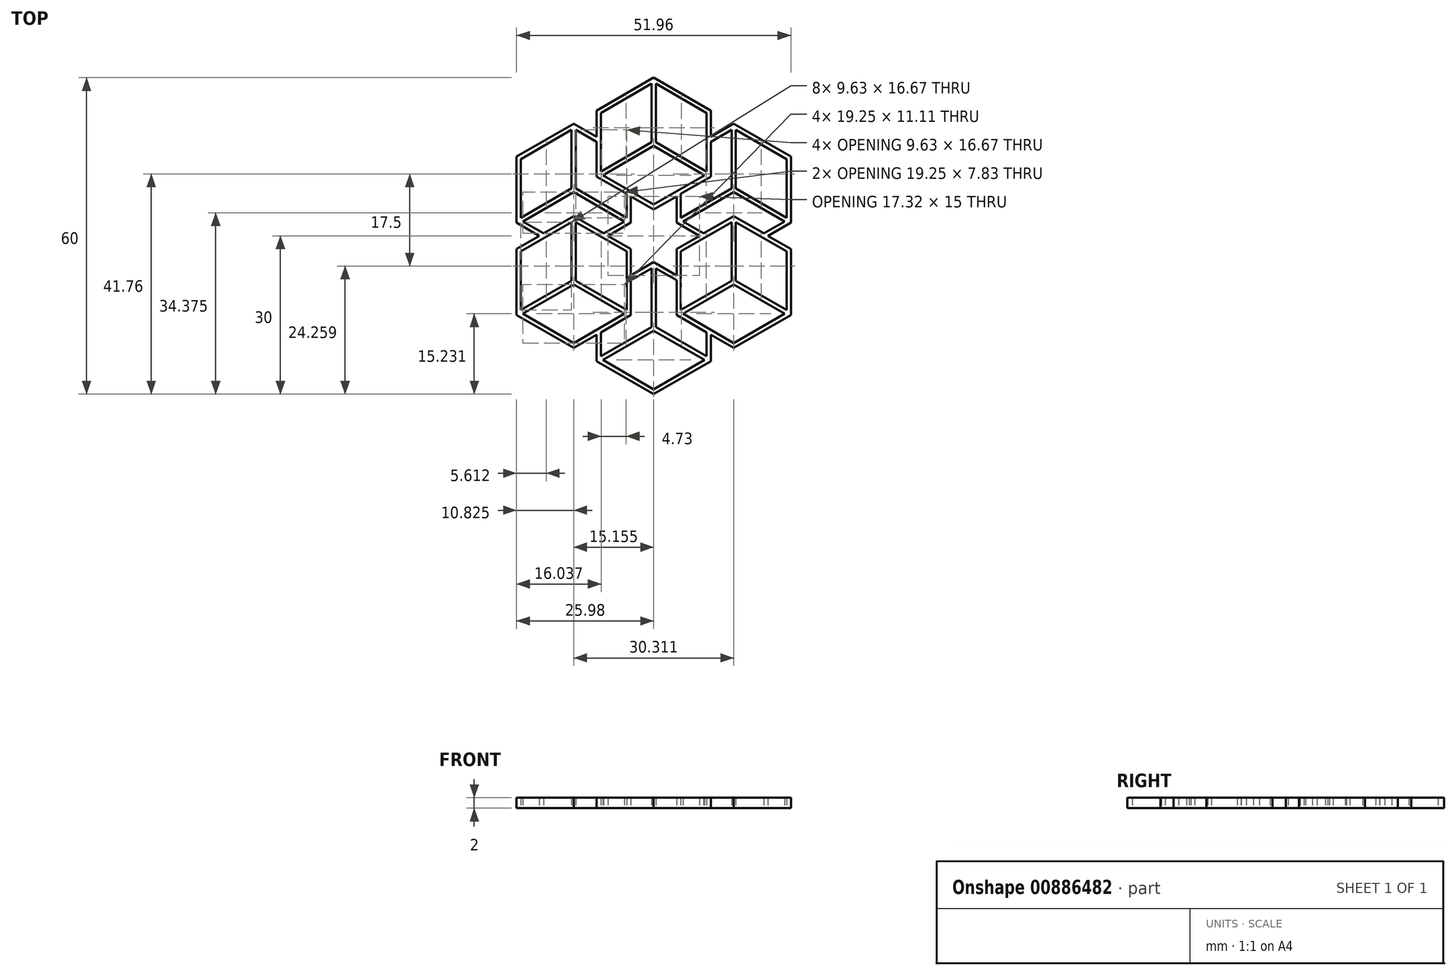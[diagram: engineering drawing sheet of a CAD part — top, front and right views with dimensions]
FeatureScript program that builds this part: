
annotation { "Feature Type Name" : "Feature", "Feature Type Description" : "" }
export const myFeature = defineFeature(function(context is Context, id is Id, definition is map)
    precondition{}
    {
        {
            var Q0;
            Q0=qCreatedBy(makeId("Top.planeOp"),FACE);
            var sketch = newSketch(context, id + "F0", { "sketchPlane" : qUnion([Q0])});
            skCircle(sketch, "E0.cCircle", {"center": v(0, 0) * mm, "radius": 30 * mm, "construction": true});
            skLineSegment(sketch, "E0.0", {"start": v(-25.98, 15) * mm, "end": v(0, 30) * mm, "construction": true});
            skLineSegment(sketch, "E0.1", {"start": v(0, 30) * mm, "end": v(25.98, 15) * mm, "construction": true});
            skLineSegment(sketch, "E0.2", {"start": v(25.98, 15) * mm, "end": v(25.98, -15) * mm, "construction": true});
            skLineSegment(sketch, "E0.3", {"start": v(25.98, -15) * mm, "end": v(0, -30) * mm, "construction": true});
            skLineSegment(sketch, "E0.4", {"start": v(0, -30) * mm, "end": v(-25.98, -15) * mm, "construction": true});
            skLineSegment(sketch, "E0.5", {"start": v(-25.98, -15) * mm, "end": v(-25.98, 15) * mm, "construction": true});
            skCircle(sketch, "E1.cCircle", {"center": v(0, -17.5) * mm, "radius": 12.5 * mm, "construction": true});
            skLineSegment(sketch, "E1.0", {"start": v(0, -30) * mm, "end": v(-10.83, -23.75) * mm});
            skLineSegment(sketch, "E1.1", {"start": v(-10.83, -23.75) * mm, "end": v(-10.83, -11.25) * mm});
            skLineSegment(sketch, "E1.2", {"start": v(-10.83, -11.25) * mm, "end": v(0, -5) * mm});
            skLineSegment(sketch, "E1.3", {"start": v(0, -5) * mm, "end": v(10.83, -11.25) * mm});
            skLineSegment(sketch, "E1.4", {"start": v(10.83, -11.25) * mm, "end": v(10.83, -23.75) * mm});
            skLineSegment(sketch, "E1.5", {"start": v(10.83, -23.75) * mm, "end": v(0, -30) * mm});
            skCircle(sketch, "E2.cCircle", {"center": v(0, -17.5) * mm, "radius": 11.58 * mm, "construction": true});
            skLineSegment(sketch, "E2.0", {"start": v(0.4, -6.15) * mm, "end": v(10.03, -11.71) * mm});
            skLineSegment(sketch, "E2.1", {"start": v(10.03, -11.71) * mm, "end": v(10.03, -22.83) * mm});
            skLineSegment(sketch, "E2.2", {"start": v(9.63, -23.52) * mm, "end": v(0, -29.08) * mm});
            skLineSegment(sketch, "E2.3", {"start": v(0, -29.08) * mm, "end": v(-9.63, -23.52) * mm});
            skLineSegment(sketch, "E2.4", {"start": v(-10.03, -22.83) * mm, "end": v(-10.03, -11.71) * mm});
            skLineSegment(sketch, "E2.5", {"start": v(-10.03, -11.71) * mm, "end": v(-0.4, -6.15) * mm});
            skLineSegment(sketch, "E3.0", {"start": v(0, -17.96) * mm, "end": v(9.63, -23.52) * mm});
            skLineSegment(sketch, "E4.0", {"start": v(0.4, -17.27) * mm, "end": v(10.03, -22.83) * mm});
            skLineSegment(sketch, "E5.0", {"start": v(-0.4, -17.27) * mm, "end": v(-10.03, -22.83) * mm});
            skLineSegment(sketch, "E6.0", {"start": v(0, -17.96) * mm, "end": v(-9.63, -23.52) * mm});
            skPoint(sketch, "E7.orphan", {"position": v(-10.03, -23.29) * mm});
            skLineSegment(sketch, "E8.trimOffspring", {"start": v(-0.4, -6.15) * mm, "end": v(-0.4, -17.27) * mm});
            skLineSegment(sketch, "E9.trimOffspring", {"start": v(0.4, -6.15) * mm, "end": v(0.4, -17.27) * mm});
            skPoint(sketch, "E10.orphan", {"position": v(0, -5.92) * mm});
            skLineSegment(sketch, "E11", {"start": v(0, -17.5) * mm, "end": v(10.83, -23.75) * mm, "construction": true});
            skLineSegment(sketch, "E12", {"start": v(0, -17.5) * mm, "end": v(-10.83, -23.75) * mm, "construction": true});
            skCircle(sketch, "E13.cCircle", {"center": v(15.16, -8.75) * mm, "radius": 12.5 * mm, "construction": true});
            skLineSegment(sketch, "E13.0", {"start": v(15.16, -21.25) * mm, "end": v(4.33, -15) * mm});
            skLineSegment(sketch, "E13.1", {"start": v(4.33, -15) * mm, "end": v(4.33, -2.5) * mm});
            skLineSegment(sketch, "E13.2", {"start": v(4.33, -2.5) * mm, "end": v(15.16, 3.75) * mm});
            skLineSegment(sketch, "E13.3", {"start": v(15.16, 3.75) * mm, "end": v(25.98, -2.5) * mm});
            skLineSegment(sketch, "E13.4", {"start": v(25.98, -2.5) * mm, "end": v(25.98, -15) * mm});
            skLineSegment(sketch, "E13.5", {"start": v(25.98, -15) * mm, "end": v(15.16, -21.25) * mm});
            skCircle(sketch, "E14.cCircle", {"center": v(15.16, -8.75) * mm, "radius": 11.58 * mm, "construction": true});
            skLineSegment(sketch, "E14.0", {"start": v(15.56, 2.6) * mm, "end": v(25.18, -2.96) * mm});
            skLineSegment(sketch, "E14.1", {"start": v(25.18, -2.96) * mm, "end": v(25.18, -14.08) * mm});
            skLineSegment(sketch, "E14.2", {"start": v(24.78, -14.77) * mm, "end": v(15.16, -20.33) * mm});
            skLineSegment(sketch, "E14.3", {"start": v(15.16, -20.33) * mm, "end": v(5.53, -14.77) * mm});
            skLineSegment(sketch, "E14.4", {"start": v(5.13, -14.08) * mm, "end": v(5.13, -2.96) * mm});
            skLineSegment(sketch, "E14.5", {"start": v(5.13, -2.96) * mm, "end": v(14.76, 2.6) * mm});
            skLineSegment(sketch, "E15.0", {"start": v(15.16, -9.21) * mm, "end": v(24.78, -14.77) * mm});
            skLineSegment(sketch, "E16.0", {"start": v(15.56, -8.52) * mm, "end": v(25.18, -14.08) * mm});
            skLineSegment(sketch, "E17.0", {"start": v(14.76, -8.52) * mm, "end": v(5.13, -14.08) * mm});
            skLineSegment(sketch, "E18.0", {"start": v(15.16, -9.21) * mm, "end": v(5.53, -14.77) * mm});
            skPoint(sketch, "E19.orphan", {"position": v(5.13, -14.54) * mm});
            skLineSegment(sketch, "E20.trimOffspring", {"start": v(14.76, 2.6) * mm, "end": v(14.76, -8.52) * mm});
            skLineSegment(sketch, "E21.trimOffspring", {"start": v(15.56, 2.6) * mm, "end": v(15.56, -8.52) * mm});
            skPoint(sketch, "E22.orphan", {"position": v(15.16, 2.83) * mm});
            skLineSegment(sketch, "E23", {"start": v(15.16, -8.75) * mm, "end": v(25.98, -15) * mm, "construction": true});
            skLineSegment(sketch, "E24", {"start": v(15.16, -8.75) * mm, "end": v(4.33, -15) * mm, "construction": true});
            skCircle(sketch, "E25.cCircle", {"center": v(-15.16, -8.75) * mm, "radius": 12.5 * mm, "construction": true});
            skLineSegment(sketch, "E25.0", {"start": v(-15.16, -21.25) * mm, "end": v(-25.98, -15) * mm});
            skLineSegment(sketch, "E25.1", {"start": v(-25.98, -15) * mm, "end": v(-25.98, -2.5) * mm});
            skLineSegment(sketch, "E25.2", {"start": v(-25.98, -2.5) * mm, "end": v(-15.16, 3.75) * mm});
            skLineSegment(sketch, "E25.3", {"start": v(-15.16, 3.75) * mm, "end": v(-4.33, -2.5) * mm});
            skLineSegment(sketch, "E25.4", {"start": v(-4.33, -2.5) * mm, "end": v(-4.33, -15) * mm});
            skLineSegment(sketch, "E25.5", {"start": v(-4.33, -15) * mm, "end": v(-15.16, -21.25) * mm});
            skCircle(sketch, "E26.cCircle", {"center": v(-15.16, -8.75) * mm, "radius": 11.58 * mm, "construction": true});
            skLineSegment(sketch, "E26.0", {"start": v(-14.76, 2.6) * mm, "end": v(-5.13, -2.96) * mm});
            skLineSegment(sketch, "E26.1", {"start": v(-5.13, -2.96) * mm, "end": v(-5.13, -14.08) * mm});
            skLineSegment(sketch, "E26.2", {"start": v(-5.53, -14.77) * mm, "end": v(-15.16, -20.33) * mm});
            skLineSegment(sketch, "E26.3", {"start": v(-15.16, -20.33) * mm, "end": v(-24.78, -14.77) * mm});
            skLineSegment(sketch, "E26.4", {"start": v(-25.18, -14.08) * mm, "end": v(-25.18, -2.96) * mm});
            skLineSegment(sketch, "E26.5", {"start": v(-25.18, -2.96) * mm, "end": v(-15.56, 2.6) * mm});
            skLineSegment(sketch, "E27.0", {"start": v(-15.16, -9.21) * mm, "end": v(-5.53, -14.77) * mm});
            skLineSegment(sketch, "E28.0", {"start": v(-14.76, -8.52) * mm, "end": v(-5.13, -14.08) * mm});
            skLineSegment(sketch, "E29.0", {"start": v(-15.56, -8.52) * mm, "end": v(-25.18, -14.08) * mm});
            skLineSegment(sketch, "E30.0", {"start": v(-15.16, -9.21) * mm, "end": v(-24.78, -14.77) * mm});
            skPoint(sketch, "E31.orphan", {"position": v(-25.18, -14.54) * mm});
            skLineSegment(sketch, "E32.trimOffspring", {"start": v(-15.56, 2.6) * mm, "end": v(-15.56, -8.52) * mm});
            skLineSegment(sketch, "E33.trimOffspring", {"start": v(-14.76, 2.6) * mm, "end": v(-14.76, -8.52) * mm});
            skPoint(sketch, "E34.orphan", {"position": v(-15.16, 2.83) * mm});
            skLineSegment(sketch, "E35", {"start": v(-15.16, -8.75) * mm, "end": v(-4.33, -15) * mm, "construction": true});
            skLineSegment(sketch, "E36", {"start": v(-15.16, -8.75) * mm, "end": v(-25.98, -15) * mm, "construction": true});
            skCircle(sketch, "E37.cCircle", {"center": v(0, 17.5) * mm, "radius": 12.5 * mm, "construction": true});
            skLineSegment(sketch, "E37.0", {"start": v(0, 5) * mm, "end": v(-10.83, 11.25) * mm});
            skLineSegment(sketch, "E37.1", {"start": v(-10.83, 11.25) * mm, "end": v(-10.83, 23.75) * mm});
            skLineSegment(sketch, "E37.2", {"start": v(-10.83, 23.75) * mm, "end": v(0, 30) * mm});
            skLineSegment(sketch, "E37.3", {"start": v(0, 30) * mm, "end": v(10.83, 23.75) * mm});
            skLineSegment(sketch, "E37.4", {"start": v(10.83, 23.75) * mm, "end": v(10.83, 11.25) * mm});
            skLineSegment(sketch, "E37.5", {"start": v(10.83, 11.25) * mm, "end": v(0, 5) * mm});
            skCircle(sketch, "E38.cCircle", {"center": v(0, 17.5) * mm, "radius": 11.58 * mm, "construction": true});
            skLineSegment(sketch, "E38.0", {"start": v(0.4, 28.85) * mm, "end": v(10.03, 23.29) * mm});
            skLineSegment(sketch, "E38.1", {"start": v(10.03, 23.29) * mm, "end": v(10.03, 12.17) * mm});
            skLineSegment(sketch, "E38.2", {"start": v(9.63, 11.48) * mm, "end": v(0, 5.92) * mm});
            skLineSegment(sketch, "E38.3", {"start": v(0, 5.92) * mm, "end": v(-9.63, 11.48) * mm});
            skLineSegment(sketch, "E38.4", {"start": v(-10.03, 12.17) * mm, "end": v(-10.03, 23.29) * mm});
            skLineSegment(sketch, "E38.5", {"start": v(-10.03, 23.29) * mm, "end": v(-0.4, 28.85) * mm});
            skLineSegment(sketch, "E39.0", {"start": v(0, 17.04) * mm, "end": v(9.63, 11.48) * mm});
            skLineSegment(sketch, "E40.0", {"start": v(0.4, 17.73) * mm, "end": v(10.03, 12.17) * mm});
            skLineSegment(sketch, "E41.0", {"start": v(-0.4, 17.73) * mm, "end": v(-10.03, 12.17) * mm});
            skLineSegment(sketch, "E42.0", {"start": v(0, 17.04) * mm, "end": v(-9.63, 11.48) * mm});
            skLineSegment(sketch, "E43.trimOffspring", {"start": v(-0.4, 28.85) * mm, "end": v(-0.4, 17.73) * mm});
            skLineSegment(sketch, "E44.trimOffspring", {"start": v(0.4, 28.85) * mm, "end": v(0.4, 17.73) * mm});
            skPoint(sketch, "E45.orphan", {"position": v(0, 29.08) * mm});
            skLineSegment(sketch, "E46", {"start": v(0, 17.5) * mm, "end": v(10.83, 11.25) * mm, "construction": true});
            skLineSegment(sketch, "E47", {"start": v(0, 17.5) * mm, "end": v(-10.83, 11.25) * mm, "construction": true});
            skCircle(sketch, "E48.cCircle", {"center": v(-15.16, 8.75) * mm, "radius": 12.5 * mm, "construction": true});
            skLineSegment(sketch, "E48.0", {"start": v(-15.16, -3.75) * mm, "end": v(-25.98, 2.5) * mm});
            skLineSegment(sketch, "E48.1", {"start": v(-25.98, 2.5) * mm, "end": v(-25.98, 15) * mm});
            skLineSegment(sketch, "E48.2", {"start": v(-25.98, 15) * mm, "end": v(-15.16, 21.25) * mm});
            skLineSegment(sketch, "E48.3", {"start": v(-15.16, 21.25) * mm, "end": v(-4.33, 15) * mm});
            skLineSegment(sketch, "E48.4", {"start": v(-4.33, 15) * mm, "end": v(-4.33, 2.5) * mm});
            skLineSegment(sketch, "E48.5", {"start": v(-4.33, 2.5) * mm, "end": v(-15.16, -3.75) * mm});
            skCircle(sketch, "E49.cCircle", {"center": v(-15.16, 8.75) * mm, "radius": 11.58 * mm, "construction": true});
            skLineSegment(sketch, "E49.0", {"start": v(-14.76, 20.1) * mm, "end": v(-5.13, 14.54) * mm});
            skLineSegment(sketch, "E49.1", {"start": v(-5.13, 14.54) * mm, "end": v(-5.13, 3.42) * mm});
            skLineSegment(sketch, "E49.2", {"start": v(-5.53, 2.73) * mm, "end": v(-15.16, -2.83) * mm});
            skLineSegment(sketch, "E49.3", {"start": v(-15.16, -2.83) * mm, "end": v(-24.78, 2.73) * mm});
            skLineSegment(sketch, "E49.4", {"start": v(-25.18, 3.42) * mm, "end": v(-25.18, 14.54) * mm});
            skLineSegment(sketch, "E49.5", {"start": v(-25.18, 14.54) * mm, "end": v(-15.56, 20.1) * mm});
            skLineSegment(sketch, "E50.0", {"start": v(-15.16, 8.29) * mm, "end": v(-5.53, 2.73) * mm});
            skLineSegment(sketch, "E51.0", {"start": v(-14.76, 8.98) * mm, "end": v(-5.13, 3.42) * mm});
            skLineSegment(sketch, "E52.0", {"start": v(-15.56, 8.98) * mm, "end": v(-25.18, 3.42) * mm});
            skLineSegment(sketch, "E53.0", {"start": v(-15.16, 8.29) * mm, "end": v(-24.78, 2.73) * mm});
            skPoint(sketch, "E54.orphan", {"position": v(-25.18, 2.96) * mm});
            skLineSegment(sketch, "E55.trimOffspring", {"start": v(-15.56, 20.1) * mm, "end": v(-15.56, 8.98) * mm});
            skLineSegment(sketch, "E56.trimOffspring", {"start": v(-14.76, 20.1) * mm, "end": v(-14.76, 8.98) * mm});
            skPoint(sketch, "E57.orphan", {"position": v(-15.16, 20.33) * mm});
            skLineSegment(sketch, "E58", {"start": v(-15.16, 8.75) * mm, "end": v(-4.33, 2.5) * mm, "construction": true});
            skLineSegment(sketch, "E59", {"start": v(-15.16, 8.75) * mm, "end": v(-25.98, 2.5) * mm, "construction": true});
            skCircle(sketch, "E60.cCircle", {"center": v(15.16, 8.75) * mm, "radius": 12.5 * mm, "construction": true});
            skLineSegment(sketch, "E60.0", {"start": v(15.16, -3.75) * mm, "end": v(4.33, 2.5) * mm});
            skLineSegment(sketch, "E60.1", {"start": v(4.33, 2.5) * mm, "end": v(4.33, 15) * mm});
            skLineSegment(sketch, "E60.2", {"start": v(4.33, 15) * mm, "end": v(15.16, 21.25) * mm});
            skLineSegment(sketch, "E60.3", {"start": v(15.16, 21.25) * mm, "end": v(25.98, 15) * mm});
            skLineSegment(sketch, "E60.4", {"start": v(25.98, 15) * mm, "end": v(25.98, 2.5) * mm});
            skLineSegment(sketch, "E60.5", {"start": v(25.98, 2.5) * mm, "end": v(15.16, -3.75) * mm});
            skCircle(sketch, "E61.cCircle", {"center": v(15.16, 8.75) * mm, "radius": 11.58 * mm, "construction": true});
            skLineSegment(sketch, "E61.0", {"start": v(15.56, 20.1) * mm, "end": v(25.18, 14.54) * mm});
            skLineSegment(sketch, "E61.1", {"start": v(25.18, 14.54) * mm, "end": v(25.18, 3.42) * mm});
            skLineSegment(sketch, "E61.2", {"start": v(24.78, 2.73) * mm, "end": v(15.16, -2.83) * mm});
            skLineSegment(sketch, "E61.3", {"start": v(15.16, -2.83) * mm, "end": v(5.53, 2.73) * mm});
            skLineSegment(sketch, "E61.4", {"start": v(5.13, 3.42) * mm, "end": v(5.13, 14.54) * mm});
            skLineSegment(sketch, "E61.5", {"start": v(5.13, 14.54) * mm, "end": v(14.76, 20.1) * mm});
            skLineSegment(sketch, "E62.0", {"start": v(15.16, 8.29) * mm, "end": v(24.78, 2.73) * mm});
            skLineSegment(sketch, "E63.0", {"start": v(15.56, 8.98) * mm, "end": v(25.18, 3.42) * mm});
            skLineSegment(sketch, "E64.0", {"start": v(14.76, 8.98) * mm, "end": v(5.13, 3.42) * mm});
            skLineSegment(sketch, "E65.0", {"start": v(15.16, 8.29) * mm, "end": v(5.53, 2.73) * mm});
            skLineSegment(sketch, "E66.trimOffspring", {"start": v(14.76, 20.1) * mm, "end": v(14.76, 8.98) * mm});
            skLineSegment(sketch, "E67.trimOffspring", {"start": v(15.56, 20.1) * mm, "end": v(15.56, 8.98) * mm});
            skPoint(sketch, "E68.orphan", {"position": v(15.16, 20.33) * mm});
            skLineSegment(sketch, "E69", {"start": v(15.16, 8.75) * mm, "end": v(25.98, 2.5) * mm, "construction": true});
            skLineSegment(sketch, "E70", {"start": v(15.16, 8.75) * mm, "end": v(4.33, 2.5) * mm, "construction": true});
            skSolve(sketch);
        }
        {
            var Q0;
            {var subQ5=sQuery(id+"F0.wireOp",EDGE,"E25.3");var subQ6=sQuery(id+"F0.wireOp",EDGE,"E25.2");var subQ7=makeQuery(id+"F0.imprint","INTERSECT",VERTEX,{"derivedFrom":[subQ6,subQ5]});Q0=makeQuery(id+"F0.imprint","IMPRINT",FACE,{"disambiguationData":[TD([[makeQuery(id+"F0.imprint","IMPRINT",EDGE,{"disambiguationData":[TD([[subQ7,1.0]])],"derivedFrom":subQ6}),-1.0]])]});}
            var Q1;
            {var subQ3=sQuery(id+"F0.wireOp",EDGE,"E25.0");Q1=makeQuery(id+"F0.imprint","IMPRINT",FACE,{"disambiguationData":[TD([[makeQuery(id+"F0.imprint","IMPRINT",EDGE,{"derivedFrom":subQ3}),-1.0]])]});}
            var Q2;
            {var subQ1=sQuery(id+"F0.wireOp",EDGE,"E2.4");var subQ11=sQuery(id+"F0.wireOp",EDGE,"E25.5");var subQ12=makeQuery(id+"F0.imprint","INTERSECT",VERTEX,{"derivedFrom":[subQ1,subQ11]});Q2=makeQuery(id+"F0.imprint","IMPRINT",FACE,{"disambiguationData":[TD([[makeQuery(id+"F0.imprint","IMPRINT",EDGE,{"disambiguationData":[TD([[subQ12,-1.0]])],"derivedFrom":subQ1}),-1.0]])]});}
            var Q3;
            {var subQ0=sQuery(id+"F0.wireOp",EDGE,"E26.1");var subQ9=sQuery(id+"F0.wireOp",EDGE,"E1.2");var subQ11=makeQuery(id+"F0.imprint","INTERSECT",VERTEX,{"derivedFrom":[subQ9,subQ0]});Q3=makeQuery(id+"F0.imprint","IMPRINT",FACE,{"disambiguationData":[TD([[makeQuery(id+"F0.imprint","IMPRINT",EDGE,{"disambiguationData":[TD([[subQ11,-1.0]])],"derivedFrom":subQ9}),1.0]])]});}
            var Q4;
            {var subQ5=sQuery(id+"F0.wireOp",EDGE,"E32.trimOffspring");var subQ9=sQuery(id+"F0.wireOp",EDGE,"E49.3");var subQ10=makeQuery(id+"F0.imprint","INTERSECT",VERTEX,{"derivedFrom":[subQ5,subQ9]});Q4=makeQuery(id+"F0.imprint","IMPRINT",FACE,{"disambiguationData":[TD([[makeQuery(id+"F0.imprint","IMPRINT",EDGE,{"disambiguationData":[TD([[subQ10,-1.0]])],"derivedFrom":subQ5}),1.0]])]});}
            var Q5;
            {var subQ0=sQuery(id+"F0.wireOp",EDGE,"E48.0");var subQ1=sQuery(id+"F0.wireOp",EDGE,"E25.2");var subQ2=makeQuery(id+"F0.imprint","INTERSECT",VERTEX,{"derivedFrom":[subQ1,subQ0]});Q5=makeQuery(id+"F0.imprint","IMPRINT",FACE,{"disambiguationData":[TD([[makeQuery(id+"F0.imprint","IMPRINT",EDGE,{"disambiguationData":[TD([[subQ2,-1.0]])],"derivedFrom":subQ1}),-1.0]])]});}
            var Q6;
            {var subQ0=sQuery(id+"F0.wireOp",EDGE,"E49.2");var subQ1=sQuery(id+"F0.wireOp",EDGE,"E25.3");var subQ2=makeQuery(id+"F0.imprint","INTERSECT",VERTEX,{"derivedFrom":[subQ1,subQ0]});Q6=makeQuery(id+"F0.imprint","IMPRINT",FACE,{"disambiguationData":[TD([[makeQuery(id+"F0.imprint","IMPRINT",EDGE,{"disambiguationData":[TD([[subQ2,-1.0]])],"derivedFrom":subQ1}),-1.0]])]});}
            var Q7;
            {var subQ9=sQuery(id+"F0.wireOp",EDGE,"E48.1");Q7=makeQuery(id+"F0.imprint","IMPRINT",FACE,{"disambiguationData":[TD([[makeQuery(id+"F0.imprint","IMPRINT",EDGE,{"derivedFrom":subQ9}),-1.0]])]});}
            var Q8;
            {var subQ0=sQuery(id+"F0.wireOp",EDGE,"E26.1");var subQ1=sQuery(id+"F0.wireOp",EDGE,"E1.2");var subQ2=makeQuery(id+"F0.imprint","INTERSECT",VERTEX,{"derivedFrom":[subQ1,subQ0]});Q8=makeQuery(id+"F0.imprint","IMPRINT",FACE,{"disambiguationData":[TD([[makeQuery(id+"F0.imprint","IMPRINT",EDGE,{"disambiguationData":[TD([[subQ2,-1.0]])],"derivedFrom":subQ1}),-1.0]])]});}
            var Q9;
            {var subQ7=sQuery(id+"F0.wireOp",EDGE,"E1.2");var subQ8=sQuery(id+"F0.wireOp",EDGE,"E1.1");var subQ9=makeQuery(id+"F0.imprint","INTERSECT",VERTEX,{"derivedFrom":[subQ8,subQ7]});Q9=makeQuery(id+"F0.imprint","IMPRINT",FACE,{"disambiguationData":[TD([[makeQuery(id+"F0.imprint","IMPRINT",EDGE,{"disambiguationData":[TD([[subQ9,1.0]])],"derivedFrom":subQ8}),-1.0]])]});}
            var Q10;
            {var subQ17=sQuery(id+"F0.wireOp",EDGE,"E1.0");Q10=makeQuery(id+"F0.imprint","IMPRINT",FACE,{"disambiguationData":[TD([[makeQuery(id+"F0.imprint","IMPRINT",EDGE,{"derivedFrom":subQ17}),-1.0]])]});}
            var Q11;
            {var subQ0=sQuery(id+"F0.wireOp",EDGE,"E25.5");var subQ1=sQuery(id+"F0.wireOp",EDGE,"E1.1");var subQ2=makeQuery(id+"F0.imprint","INTERSECT",VERTEX,{"derivedFrom":[subQ1,subQ0]});Q11=makeQuery(id+"F0.imprint","IMPRINT",FACE,{"disambiguationData":[TD([[makeQuery(id+"F0.imprint","IMPRINT",EDGE,{"disambiguationData":[TD([[subQ2,-1.0]])],"derivedFrom":subQ1}),-1.0]])]});}
            var Q12;
            {var subQ5=sQuery(id+"F0.wireOp",EDGE,"E37.1");var subQ6=sQuery(id+"F0.wireOp",EDGE,"E37.0");var subQ7=makeQuery(id+"F0.imprint","INTERSECT",VERTEX,{"derivedFrom":[subQ6,subQ5]});Q12=makeQuery(id+"F0.imprint","IMPRINT",FACE,{"disambiguationData":[TD([[makeQuery(id+"F0.imprint","IMPRINT",EDGE,{"disambiguationData":[TD([[subQ7,1.0]])],"derivedFrom":subQ6}),-1.0]])]});}
            var Q13;
            {var subQ0=sQuery(id+"F0.wireOp",EDGE,"E48.4");var subQ1=sQuery(id+"F0.wireOp",EDGE,"E37.0");var subQ2=makeQuery(id+"F0.imprint","INTERSECT",VERTEX,{"derivedFrom":[subQ1,subQ0]});Q13=makeQuery(id+"F0.imprint","IMPRINT",FACE,{"disambiguationData":[TD([[makeQuery(id+"F0.imprint","IMPRINT",EDGE,{"disambiguationData":[TD([[subQ2,-1.0]])],"derivedFrom":subQ1}),-1.0]])]});}
            var Q14;
            {var subQ0=sQuery(id+"F0.wireOp",EDGE,"E48.3");var subQ1=sQuery(id+"F0.wireOp",EDGE,"E37.1");var subQ2=makeQuery(id+"F0.imprint","INTERSECT",VERTEX,{"derivedFrom":[subQ1,subQ0]});Q14=makeQuery(id+"F0.imprint","IMPRINT",FACE,{"disambiguationData":[TD([[makeQuery(id+"F0.imprint","IMPRINT",EDGE,{"disambiguationData":[TD([[subQ2,1.0]])],"derivedFrom":subQ1}),-1.0]])]});}
            var Q15;
            {var subQ1=sQuery(id+"F0.wireOp",EDGE,"E48.3");var subQ8=sQuery(id+"F0.wireOp",EDGE,"E41.0");var subQ10=makeQuery(id+"F0.imprint","INTERSECT",VERTEX,{"derivedFrom":[subQ8,subQ1]});Q15=makeQuery(id+"F0.imprint","IMPRINT",FACE,{"disambiguationData":[TD([[makeQuery(id+"F0.imprint","IMPRINT",EDGE,{"disambiguationData":[TD([[subQ10,-1.0]])],"derivedFrom":subQ8}),1.0]])]});}
            var Q16;
            {var subQ21=sQuery(id+"F0.wireOp",EDGE,"E37.2");Q16=makeQuery(id+"F0.imprint","IMPRINT",FACE,{"disambiguationData":[TD([[makeQuery(id+"F0.imprint","IMPRINT",EDGE,{"derivedFrom":subQ21}),-1.0]])]});}
            var Q17;
            {var subQ5=sQuery(id+"F0.wireOp",EDGE,"E37.0");var subQ7=sQuery(id+"F0.wireOp",EDGE,"E37.5");var subQ8=makeQuery(id+"F0.imprint","INTERSECT",VERTEX,{"derivedFrom":[subQ5,subQ7]});Q17=makeQuery(id+"F0.imprint","IMPRINT",FACE,{"disambiguationData":[TD([[makeQuery(id+"F0.imprint","IMPRINT",EDGE,{"disambiguationData":[TD([[subQ8,-1.0]])],"derivedFrom":subQ5}),-1.0]])]});}
            var Q18;
            {var subQ0=sQuery(id+"F0.wireOp",EDGE,"E61.4");var subQ1=sQuery(id+"F0.wireOp",EDGE,"E37.5");var subQ2=makeQuery(id+"F0.imprint","INTERSECT",VERTEX,{"derivedFrom":[subQ1,subQ0]});Q18=makeQuery(id+"F0.imprint","IMPRINT",FACE,{"disambiguationData":[TD([[makeQuery(id+"F0.imprint","IMPRINT",EDGE,{"disambiguationData":[TD([[subQ2,-1.0]])],"derivedFrom":subQ1}),-1.0]])]});}
            var Q19;
            {var subQ12=sQuery(id+"F0.wireOp",EDGE,"E37.5");var subQ13=sQuery(id+"F0.wireOp",EDGE,"E37.4");var subQ14=makeQuery(id+"F0.imprint","INTERSECT",VERTEX,{"derivedFrom":[subQ13,subQ12]});Q19=makeQuery(id+"F0.imprint","IMPRINT",FACE,{"disambiguationData":[TD([[makeQuery(id+"F0.imprint","IMPRINT",EDGE,{"disambiguationData":[TD([[subQ14,1.0]])],"derivedFrom":subQ13}),-1.0]])]});}
            var Q20;
            {var subQ1=sQuery(id+"F0.wireOp",EDGE,"E60.1");var subQ3=sQuery(id+"F0.wireOp",EDGE,"E39.0");var subQ4=makeQuery(id+"F0.imprint","INTERSECT",VERTEX,{"derivedFrom":[subQ3,subQ1]});Q20=makeQuery(id+"F0.imprint","IMPRINT",FACE,{"disambiguationData":[TD([[makeQuery(id+"F0.imprint","IMPRINT",EDGE,{"disambiguationData":[TD([[subQ4,-1.0]])],"derivedFrom":subQ3}),1.0]])]});}
            var Q21;
            {var subQ0=sQuery(id+"F0.wireOp",EDGE,"E60.3");Q21=makeQuery(id+"F0.imprint","IMPRINT",FACE,{"disambiguationData":[TD([[makeQuery(id+"F0.imprint","IMPRINT",EDGE,{"derivedFrom":subQ0}),-1.0]])]});}
            var Q22;
            {var subQ0=sQuery(id+"F0.wireOp",EDGE,"E60.2");var subQ1=sQuery(id+"F0.wireOp",EDGE,"E37.4");var subQ2=makeQuery(id+"F0.imprint","INTERSECT",VERTEX,{"derivedFrom":[subQ1,subQ0]});Q22=makeQuery(id+"F0.imprint","IMPRINT",FACE,{"disambiguationData":[TD([[makeQuery(id+"F0.imprint","IMPRINT",EDGE,{"disambiguationData":[TD([[subQ2,-1.0]])],"derivedFrom":subQ1}),-1.0]])]});}
            var Q23;
            {var subQ0=sQuery(id+"F0.wireOp",EDGE,"E60.0");var subQ1=sQuery(id+"F0.wireOp",EDGE,"E13.2");var subQ2=makeQuery(id+"F0.imprint","INTERSECT",VERTEX,{"derivedFrom":[subQ1,subQ0]});Q23=makeQuery(id+"F0.imprint","IMPRINT",FACE,{"disambiguationData":[TD([[makeQuery(id+"F0.imprint","IMPRINT",EDGE,{"disambiguationData":[TD([[subQ2,-1.0]])],"derivedFrom":subQ1}),-1.0]])]});}
            var Q24;
            {var subQ12=sQuery(id+"F0.wireOp",EDGE,"E13.3");var subQ13=sQuery(id+"F0.wireOp",EDGE,"E13.2");var subQ14=makeQuery(id+"F0.imprint","INTERSECT",VERTEX,{"derivedFrom":[subQ13,subQ12]});Q24=makeQuery(id+"F0.imprint","IMPRINT",FACE,{"disambiguationData":[TD([[makeQuery(id+"F0.imprint","IMPRINT",EDGE,{"disambiguationData":[TD([[subQ14,1.0]])],"derivedFrom":subQ13}),-1.0]])]});}
            var Q25;
            {var subQ3=sQuery(id+"F0.wireOp",EDGE,"E20.trimOffspring");var subQ9=sQuery(id+"F0.wireOp",EDGE,"E61.3");var subQ10=makeQuery(id+"F0.imprint","INTERSECT",VERTEX,{"derivedFrom":[subQ3,subQ9]});Q25=makeQuery(id+"F0.imprint","IMPRINT",FACE,{"disambiguationData":[TD([[makeQuery(id+"F0.imprint","IMPRINT",EDGE,{"disambiguationData":[TD([[subQ10,-1.0]])],"derivedFrom":subQ3}),1.0]])]});}
            var Q26;
            {var subQ0=sQuery(id+"F0.wireOp",EDGE,"E60.5");var subQ1=sQuery(id+"F0.wireOp",EDGE,"E13.3");var subQ2=makeQuery(id+"F0.imprint","INTERSECT",VERTEX,{"derivedFrom":[subQ1,subQ0]});Q26=makeQuery(id+"F0.imprint","IMPRINT",FACE,{"disambiguationData":[TD([[makeQuery(id+"F0.imprint","IMPRINT",EDGE,{"disambiguationData":[TD([[subQ2,1.0]])],"derivedFrom":subQ1}),-1.0]])]});}
            var Q27;
            {var subQ14=sQuery(id+"F0.wireOp",EDGE,"E13.4");Q27=makeQuery(id+"F0.imprint","IMPRINT",FACE,{"disambiguationData":[TD([[makeQuery(id+"F0.imprint","IMPRINT",EDGE,{"derivedFrom":subQ14}),-1.0]])]});}
            var Q28;
            {var subQ3=sQuery(id+"F0.wireOp",EDGE,"E1.3");var subQ6=sQuery(id+"F0.wireOp",EDGE,"E13.1");var subQ10=makeQuery(id+"F0.imprint","INTERSECT",VERTEX,{"derivedFrom":[subQ3,subQ6]});Q28=makeQuery(id+"F0.imprint","IMPRINT",FACE,{"disambiguationData":[TD([[makeQuery(id+"F0.imprint","IMPRINT",EDGE,{"disambiguationData":[TD([[subQ10,-1.0]])],"derivedFrom":subQ3}),1.0]])]});}
            var Q29;
            {var subQ0=sQuery(id+"F0.wireOp",EDGE,"E13.1");var subQ1=sQuery(id+"F0.wireOp",EDGE,"E1.3");var subQ2=makeQuery(id+"F0.imprint","INTERSECT",VERTEX,{"derivedFrom":[subQ1,subQ0]});Q29=makeQuery(id+"F0.imprint","IMPRINT",FACE,{"disambiguationData":[TD([[makeQuery(id+"F0.imprint","IMPRINT",EDGE,{"disambiguationData":[TD([[subQ2,-1.0]])],"derivedFrom":subQ1}),-1.0]])]});}
            var Q30;
            {var subQ1=sQuery(id+"F0.wireOp",EDGE,"E2.0");var subQ5=sQuery(id+"F0.wireOp",EDGE,"E13.1");var subQ14=makeQuery(id+"F0.imprint","INTERSECT",VERTEX,{"derivedFrom":[subQ1,subQ5]});Q30=makeQuery(id+"F0.imprint","IMPRINT",FACE,{"disambiguationData":[TD([[makeQuery(id+"F0.imprint","IMPRINT",EDGE,{"disambiguationData":[TD([[subQ14,-1.0]])],"derivedFrom":subQ1}),-1.0]])]});}
            var Q31;
            {var subQ0=sQuery(id+"F0.wireOp",EDGE,"E13.0");var subQ1=sQuery(id+"F0.wireOp",EDGE,"E1.4");var subQ2=makeQuery(id+"F0.imprint","INTERSECT",VERTEX,{"derivedFrom":[subQ1,subQ0]});Q31=makeQuery(id+"F0.imprint","IMPRINT",FACE,{"disambiguationData":[TD([[makeQuery(id+"F0.imprint","IMPRINT",EDGE,{"disambiguationData":[TD([[subQ2,1.0]])],"derivedFrom":subQ1}),-1.0]])]});}
            var Q32;
            {var subQ6=sQuery(id+"F0.wireOp",EDGE,"E1.4");var subQ9=sQuery(id+"F0.wireOp",EDGE,"E1.3");var subQ10=makeQuery(id+"F0.imprint","INTERSECT",VERTEX,{"derivedFrom":[subQ9,subQ6]});Q32=makeQuery(id+"F0.imprint","IMPRINT",FACE,{"disambiguationData":[TD([[makeQuery(id+"F0.imprint","IMPRINT",EDGE,{"disambiguationData":[TD([[subQ10,1.0]])],"derivedFrom":subQ9}),-1.0]])]});}
            var Q33;
            {var subQ3=sQuery(id+"F0.wireOp",EDGE,"E2.1");var subQ7=sQuery(id+"F0.wireOp",EDGE,"E2.0");var subQ8=makeQuery(id+"F0.imprint","INTERSECT",VERTEX,{"derivedFrom":[subQ7,subQ3]});Q33=makeQuery(id+"F0.imprint","IMPRINT",FACE,{"disambiguationData":[TD([[makeQuery(id+"F0.imprint","IMPRINT",EDGE,{"disambiguationData":[TD([[subQ8,1.0]])],"derivedFrom":subQ7}),-1.0]])]});}
            var Q34;
            {var subQ5=sQuery(id+"F0.wireOp",EDGE,"E1.3");var subQ6=sQuery(id+"F0.wireOp",EDGE,"E1.2");var subQ7=makeQuery(id+"F0.imprint","INTERSECT",VERTEX,{"derivedFrom":[subQ6,subQ5]});Q34=makeQuery(id+"F0.imprint","IMPRINT",FACE,{"disambiguationData":[TD([[makeQuery(id+"F0.imprint","IMPRINT",EDGE,{"disambiguationData":[TD([[subQ7,1.0]])],"derivedFrom":subQ6}),-1.0]])]});}
            var Q35;
            {var subQ5=sQuery(id+"F0.wireOp",EDGE,"E2.0");var subQ7=sQuery(id+"F0.wireOp",EDGE,"fe7c7291-770d-4a74-9fde-94e01091e8e7.2");var subQ9=makeQuery(id+"F0.imprint","INTERSECT",VERTEX,{"derivedFrom":[subQ5,subQ7]});Q35=makeQuery(id+"F0.imprint","IMPRINT",FACE,{"disambiguationData":[TD([[makeQuery(id+"F0.imprint","IMPRINT",EDGE,{"disambiguationData":[TD([[subQ9,-1.0]])],"derivedFrom":subQ5}),-1.0]])]});}
            var Q36;
            {var subQ5=sQuery(id+"F0.wireOp",EDGE,"E13.2");var subQ6=sQuery(id+"F0.wireOp",EDGE,"E13.1");var subQ7=makeQuery(id+"F0.imprint","INTERSECT",VERTEX,{"derivedFrom":[subQ6,subQ5]});Q36=makeQuery(id+"F0.imprint","IMPRINT",FACE,{"disambiguationData":[TD([[makeQuery(id+"F0.imprint","IMPRINT",EDGE,{"disambiguationData":[TD([[subQ7,1.0]])],"derivedFrom":subQ6}),-1.0]])]});}
            var Q37;
            {var subQ0=sQuery(id+"F0.wireOp",EDGE,"5f94be97-0224-4d17-be68-8b44869080e5.0");var subQ1=sQuery(id+"F0.wireOp",EDGE,"E13.2");var subQ2=makeQuery(id+"F0.imprint","INTERSECT",VERTEX,{"derivedFrom":[subQ1,subQ0]});Q37=makeQuery(id+"F0.imprint","IMPRINT",FACE,{"disambiguationData":[TD([[makeQuery(id+"F0.imprint","IMPRINT",EDGE,{"disambiguationData":[TD([[subQ2,-1.0]])],"derivedFrom":subQ1}),-1.0]])]});}
            var Q38;
            {var subQ7=sQuery(id+"F0.wireOp",EDGE,"E8.trimOffspring");var subQ9=sQuery(id+"F0.wireOp",EDGE,"fe7c7291-770d-4a74-9fde-94e01091e8e7.3");var subQ10=makeQuery(id+"F0.imprint","INTERSECT",VERTEX,{"derivedFrom":[subQ7,subQ9]});Q38=makeQuery(id+"F0.imprint","IMPRINT",FACE,{"disambiguationData":[TD([[makeQuery(id+"F0.imprint","IMPRINT",EDGE,{"disambiguationData":[TD([[subQ10,-1.0]])],"derivedFrom":subQ7}),1.0]])]});}
            var Q39;
            {var subQ0=sQuery(id+"F0.wireOp",EDGE,"E26.1");var subQ1=sQuery(id+"F0.wireOp",EDGE,"E2.5");var subQ2=makeQuery(id+"F0.imprint","INTERSECT",VERTEX,{"derivedFrom":[subQ1,subQ0]});Q39=makeQuery(id+"F0.imprint","IMPRINT",FACE,{"disambiguationData":[TD([[makeQuery(id+"F0.imprint","IMPRINT",EDGE,{"disambiguationData":[TD([[subQ2,-1.0]])],"derivedFrom":subQ1}),-1.0]])]});}
            var Q40;
            {var subQ0=sQuery(id+"F0.wireOp",EDGE,"fe7c7291-770d-4a74-9fde-94e01091e8e7.3");var subQ1=sQuery(id+"F0.wireOp",EDGE,"E2.5");var subQ2=makeQuery(id+"F0.imprint","INTERSECT",VERTEX,{"derivedFrom":[subQ1,subQ0]});Q40=makeQuery(id+"F0.imprint","IMPRINT",FACE,{"disambiguationData":[TD([[makeQuery(id+"F0.imprint","IMPRINT",EDGE,{"disambiguationData":[TD([[subQ2,-1.0]])],"derivedFrom":subQ1}),-1.0]])]});}
            var Q41;
            {var subQ0=sQuery(id+"F0.wireOp",EDGE,"E26.1");var subQ1=sQuery(id+"F0.wireOp",EDGE,"E2.5");var subQ2=makeQuery(id+"F0.imprint","INTERSECT",VERTEX,{"derivedFrom":[subQ1,subQ0]});Q41=makeQuery(id+"F0.imprint","IMPRINT",FACE,{"disambiguationData":[TD([[makeQuery(id+"F0.imprint","IMPRINT",EDGE,{"disambiguationData":[TD([[subQ2,-1.0]])],"derivedFrom":subQ1}),1.0]])]});}
            var Q42;
            {var subQ0=sQuery(id+"F0.wireOp",EDGE,"0c9a6bff-b2c0-4d4d-a447-967ebe58276c.0");var subQ1=sQuery(id+"F0.wireOp",EDGE,"E2.5");var subQ2=makeQuery(id+"F0.imprint","INTERSECT",VERTEX,{"derivedFrom":[subQ1,subQ0]});Q42=makeQuery(id+"F0.imprint","IMPRINT",FACE,{"disambiguationData":[TD([[makeQuery(id+"F0.imprint","IMPRINT",EDGE,{"disambiguationData":[TD([[subQ2,-1.0]])],"derivedFrom":subQ1}),-1.0]])]});}
            var Q43;
            {var subQ0=sQuery(id+"F0.wireOp",EDGE,"E48.5");var subQ1=sQuery(id+"F0.wireOp",EDGE,"E25.3");var subQ2=makeQuery(id+"F0.imprint","INTERSECT",VERTEX,{"derivedFrom":[subQ1,subQ0]});Q43=makeQuery(id+"F0.imprint","IMPRINT",FACE,{"disambiguationData":[TD([[makeQuery(id+"F0.imprint","IMPRINT",EDGE,{"disambiguationData":[TD([[subQ2,-1.0]])],"derivedFrom":subQ1}),-1.0]])]});}
            var Q44;
            {var subQ5=sQuery(id+"F0.wireOp",EDGE,"E25.4");var subQ6=sQuery(id+"F0.wireOp",EDGE,"E25.3");var subQ7=makeQuery(id+"F0.imprint","INTERSECT",VERTEX,{"derivedFrom":[subQ6,subQ5]});Q44=makeQuery(id+"F0.imprint","IMPRINT",FACE,{"disambiguationData":[TD([[makeQuery(id+"F0.imprint","IMPRINT",EDGE,{"disambiguationData":[TD([[subQ7,1.0]])],"derivedFrom":subQ6}),-1.0]])]});}
            var Q45;
            {var subQ0=sQuery(id+"F0.wireOp",EDGE,"0c9a6bff-b2c0-4d4d-a447-967ebe58276c.1");var subQ1=sQuery(id+"F0.wireOp",EDGE,"E25.3");var subQ2=makeQuery(id+"F0.imprint","INTERSECT",VERTEX,{"derivedFrom":[subQ1,subQ0]});Q45=makeQuery(id+"F0.imprint","IMPRINT",FACE,{"disambiguationData":[TD([[makeQuery(id+"F0.imprint","IMPRINT",EDGE,{"disambiguationData":[TD([[subQ2,-1.0]])],"derivedFrom":subQ1}),-1.0]])]});}
            var Q46;
            {var subQ0=sQuery(id+"F0.wireOp",EDGE,"E49.2");var subQ1=sQuery(id+"F0.wireOp",EDGE,"E26.0");var subQ2=makeQuery(id+"F0.imprint","INTERSECT",VERTEX,{"derivedFrom":[subQ1,subQ0]});Q46=makeQuery(id+"F0.imprint","IMPRINT",FACE,{"disambiguationData":[TD([[makeQuery(id+"F0.imprint","IMPRINT",EDGE,{"disambiguationData":[TD([[subQ2,-1.0]])],"derivedFrom":subQ1}),1.0]])]});}
            var Q47;
            {var subQ0=sQuery(id+"F0.wireOp",EDGE,"fe7c7291-770d-4a74-9fde-94e01091e8e7.4");var subQ1=sQuery(id+"F0.wireOp",EDGE,"E25.3");var subQ2=makeQuery(id+"F0.imprint","INTERSECT",VERTEX,{"derivedFrom":[subQ1,subQ0]});Q47=makeQuery(id+"F0.imprint","IMPRINT",FACE,{"disambiguationData":[TD([[makeQuery(id+"F0.imprint","IMPRINT",EDGE,{"disambiguationData":[TD([[subQ2,-1.0]])],"derivedFrom":subQ1}),-1.0]])]});}
            var Q48;
            {var subQ3=sQuery(id+"F0.wireOp",EDGE,"E25.3");var subQ13=sQuery(id+"F0.wireOp",EDGE,"E49.2");var subQ14=makeQuery(id+"F0.imprint","INTERSECT",VERTEX,{"derivedFrom":[subQ3,subQ13]});Q48=makeQuery(id+"F0.imprint","IMPRINT",FACE,{"disambiguationData":[TD([[makeQuery(id+"F0.imprint","IMPRINT",EDGE,{"disambiguationData":[TD([[subQ14,-1.0]])],"derivedFrom":subQ3}),1.0]])]});}
            var Q49;
            {var subQ0=sQuery(id+"F0.wireOp",EDGE,"fe7c7291-770d-4a74-9fde-94e01091e8e7.1");var subQ1=sQuery(id+"F0.wireOp",EDGE,"E14.5");var subQ2=makeQuery(id+"F0.imprint","INTERSECT",VERTEX,{"derivedFrom":[subQ1,subQ0]});Q49=makeQuery(id+"F0.imprint","IMPRINT",FACE,{"disambiguationData":[TD([[makeQuery(id+"F0.imprint","IMPRINT",EDGE,{"disambiguationData":[TD([[subQ2,-1.0]])],"derivedFrom":subQ1}),1.0]])]});}
            var Q50;
            {var subQ1=sQuery(id+"F0.wireOp",EDGE,"E13.2");var subQ7=sQuery(id+"F0.wireOp",EDGE,"fe7c7291-770d-4a74-9fde-94e01091e8e7.1");var subQ9=makeQuery(id+"F0.imprint","INTERSECT",VERTEX,{"derivedFrom":[subQ1,subQ7]});Q50=makeQuery(id+"F0.imprint","IMPRINT",FACE,{"disambiguationData":[TD([[makeQuery(id+"F0.imprint","IMPRINT",EDGE,{"disambiguationData":[TD([[subQ9,-1.0]])],"derivedFrom":subQ1}),-1.0]])]});}
            var Q51;
            {var subQ1=sQuery(id+"F0.wireOp",EDGE,"E60.0");var subQ12=sQuery(id+"F0.wireOp",EDGE,"E13.2");var subQ13=makeQuery(id+"F0.imprint","INTERSECT",VERTEX,{"derivedFrom":[subQ12,subQ1]});Q51=makeQuery(id+"F0.imprint","IMPRINT",FACE,{"disambiguationData":[TD([[makeQuery(id+"F0.imprint","IMPRINT",EDGE,{"disambiguationData":[TD([[subQ13,-1.0]])],"derivedFrom":subQ12}),1.0]])]});}
            var Q52;
            {var subQ1=sQuery(id+"F0.wireOp",EDGE,"0c9a6bff-b2c0-4d4d-a447-967ebe58276c.3");var subQ7=sQuery(id+"F0.wireOp",EDGE,"E64.0");var subQ8=makeQuery(id+"F0.imprint","INTERSECT",VERTEX,{"derivedFrom":[subQ7,subQ1]});Q52=makeQuery(id+"F0.imprint","IMPRINT",FACE,{"disambiguationData":[TD([[makeQuery(id+"F0.imprint","IMPRINT",EDGE,{"disambiguationData":[TD([[subQ8,-1.0]])],"derivedFrom":subQ7}),1.0]])]});}
            var Q53;
            {var subQ0=sQuery(id+"F0.wireOp",EDGE,"0c9a6bff-b2c0-4d4d-a447-967ebe58276c.3");var subQ1=sQuery(id+"F0.wireOp",EDGE,"E37.5");var subQ2=makeQuery(id+"F0.imprint","INTERSECT",VERTEX,{"derivedFrom":[subQ1,subQ0]});Q53=makeQuery(id+"F0.imprint","IMPRINT",FACE,{"disambiguationData":[TD([[makeQuery(id+"F0.imprint","IMPRINT",EDGE,{"disambiguationData":[TD([[subQ2,-1.0]])],"derivedFrom":subQ1}),-1.0]])]});}
            var Q54;
            {var subQ0=sQuery(id+"F0.wireOp",EDGE,"fe7c7291-770d-4a74-9fde-94e01091e8e7.0");var subQ1=sQuery(id+"F0.wireOp",EDGE,"E37.5");var subQ2=makeQuery(id+"F0.imprint","INTERSECT",VERTEX,{"derivedFrom":[subQ1,subQ0]});Q54=makeQuery(id+"F0.imprint","IMPRINT",FACE,{"disambiguationData":[TD([[makeQuery(id+"F0.imprint","IMPRINT",EDGE,{"disambiguationData":[TD([[subQ2,-1.0]])],"derivedFrom":subQ1}),-1.0]])]});}
            var Q55;
            {var subQ0=sQuery(id+"F0.wireOp",EDGE,"E61.4");var subQ1=sQuery(id+"F0.wireOp",EDGE,"E38.2");var subQ2=makeQuery(id+"F0.imprint","INTERSECT",VERTEX,{"derivedFrom":[subQ1,subQ0]});Q55=makeQuery(id+"F0.imprint","IMPRINT",FACE,{"disambiguationData":[TD([[makeQuery(id+"F0.imprint","IMPRINT",EDGE,{"disambiguationData":[TD([[subQ2,-1.0]])],"derivedFrom":subQ1}),1.0]])]});}
            var Q56;
            {var subQ0=sQuery(id+"F0.wireOp",EDGE,"E60.1");var subQ1=sQuery(id+"F0.wireOp",EDGE,"E37.5");var subQ2=makeQuery(id+"F0.imprint","INTERSECT",VERTEX,{"derivedFrom":[subQ1,subQ0]});Q56=makeQuery(id+"F0.imprint","IMPRINT",FACE,{"disambiguationData":[TD([[makeQuery(id+"F0.imprint","IMPRINT",EDGE,{"disambiguationData":[TD([[subQ2,-1.0]])],"derivedFrom":subQ1}),-1.0]])]});}
            var Q57;
            {var subQ0=sQuery(id+"F0.wireOp",EDGE,"0ac59062-be46-4c43-8f9f-82bc203d06fa.trimOffspring");var subQ1=sQuery(id+"F0.wireOp",EDGE,"E37.0");var subQ2=makeQuery(id+"F0.imprint","INTERSECT",VERTEX,{"derivedFrom":[subQ1,subQ0]});Q57=makeQuery(id+"F0.imprint","IMPRINT",FACE,{"disambiguationData":[TD([[makeQuery(id+"F0.imprint","IMPRINT",EDGE,{"disambiguationData":[TD([[subQ2,-1.0]])],"derivedFrom":subQ1}),-1.0]])]});}
            var Q58;
            {var subQ1=sQuery(id+"F0.wireOp",EDGE,"0c9a6bff-b2c0-4d4d-a447-967ebe58276c.1");var subQ3=sQuery(id+"F0.wireOp",EDGE,"E50.0");var subQ4=makeQuery(id+"F0.imprint","INTERSECT",VERTEX,{"derivedFrom":[subQ3,subQ1]});Q58=makeQuery(id+"F0.imprint","IMPRINT",FACE,{"disambiguationData":[TD([[makeQuery(id+"F0.imprint","IMPRINT",EDGE,{"disambiguationData":[TD([[subQ4,-1.0]])],"derivedFrom":subQ3}),1.0]])]});}
            var Q59;
            {var subQ0=sQuery(id+"F0.wireOp",EDGE,"E49.1");var subQ1=sQuery(id+"F0.wireOp",EDGE,"E37.0");var subQ2=makeQuery(id+"F0.imprint","INTERSECT",VERTEX,{"derivedFrom":[subQ1,subQ0]});Q59=makeQuery(id+"F0.imprint","IMPRINT",FACE,{"disambiguationData":[TD([[makeQuery(id+"F0.imprint","IMPRINT",EDGE,{"disambiguationData":[TD([[subQ2,-1.0]])],"derivedFrom":subQ1}),-1.0]])]});}
            var Q60;
            {var subQ0=sQuery(id+"F0.wireOp",EDGE,"fe7c7291-770d-4a74-9fde-94e01091e8e7.5");var subQ1=sQuery(id+"F0.wireOp",EDGE,"E38.3");var subQ2=makeQuery(id+"F0.imprint","INTERSECT",VERTEX,{"derivedFrom":[subQ1,subQ0]});Q60=makeQuery(id+"F0.imprint","IMPRINT",FACE,{"disambiguationData":[TD([[makeQuery(id+"F0.imprint","IMPRINT",EDGE,{"disambiguationData":[TD([[subQ2,-1.0]])],"derivedFrom":subQ1}),1.0]])]});}
            var Q61;
            {var subQ1=sQuery(id+"F0.wireOp",EDGE,"E37.0");var subQ7=sQuery(id+"F0.wireOp",EDGE,"fe7c7291-770d-4a74-9fde-94e01091e8e7.5");var subQ9=makeQuery(id+"F0.imprint","INTERSECT",VERTEX,{"derivedFrom":[subQ1,subQ7]});Q61=makeQuery(id+"F0.imprint","IMPRINT",FACE,{"disambiguationData":[TD([[makeQuery(id+"F0.imprint","IMPRINT",EDGE,{"disambiguationData":[TD([[subQ9,-1.0]])],"derivedFrom":subQ1}),-1.0]])]});}
            var Q62;
            {var subQ3=sQuery(id+"F0.wireOp",EDGE,"E1.3");var subQ6=sQuery(id+"F0.wireOp",EDGE,"E13.1");var subQ10=makeQuery(id+"F0.imprint","INTERSECT",VERTEX,{"derivedFrom":[subQ3,subQ6]});Q62=makeQuery(id+"F0.imprint","IMPRINT",FACE,{"disambiguationData":[TD([[makeQuery(id+"F0.imprint","IMPRINT",EDGE,{"disambiguationData":[TD([[subQ10,-1.0]])],"derivedFrom":subQ3}),1.0]])]});}
            var Q63;
            {var subQ0=sQuery(id+"F0.wireOp",EDGE,"E26.1");var subQ9=sQuery(id+"F0.wireOp",EDGE,"E1.2");var subQ11=makeQuery(id+"F0.imprint","INTERSECT",VERTEX,{"derivedFrom":[subQ9,subQ0]});Q63=makeQuery(id+"F0.imprint","IMPRINT",FACE,{"disambiguationData":[TD([[makeQuery(id+"F0.imprint","IMPRINT",EDGE,{"disambiguationData":[TD([[subQ11,-1.0]])],"derivedFrom":subQ9}),1.0]])]});}
            var Q64;
            {var subQ0=sQuery(id+"F0.wireOp",EDGE,"E26.1");var subQ1=sQuery(id+"F0.wireOp",EDGE,"E1.2");var subQ2=makeQuery(id+"F0.imprint","INTERSECT",VERTEX,{"derivedFrom":[subQ1,subQ0]});Q64=makeQuery(id+"F0.imprint","IMPRINT",FACE,{"disambiguationData":[TD([[makeQuery(id+"F0.imprint","IMPRINT",EDGE,{"disambiguationData":[TD([[subQ2,-1.0]])],"derivedFrom":subQ1}),-1.0]])]});}
            var Q65;
            {var subQ0=sQuery(id+"F0.wireOp",EDGE,"E13.1");var subQ1=sQuery(id+"F0.wireOp",EDGE,"E1.3");var subQ2=makeQuery(id+"F0.imprint","INTERSECT",VERTEX,{"derivedFrom":[subQ1,subQ0]});Q65=makeQuery(id+"F0.imprint","IMPRINT",FACE,{"disambiguationData":[TD([[makeQuery(id+"F0.imprint","IMPRINT",EDGE,{"disambiguationData":[TD([[subQ2,-1.0]])],"derivedFrom":subQ1}),-1.0]])]});}
            extrude(context, id + "F1", {"entities" : qUnion([Q0, Q1, Q2, Q3, Q4, Q5, Q6, Q7, Q8, Q9, Q10, Q11, Q12, Q13, Q14, Q15, Q16, Q17, Q18, Q19, Q20, Q21, Q22, Q23, Q24, Q25, Q26, Q27, Q28, Q29, Q30, Q31, Q32, Q33, Q34, Q35, Q36, Q37, Q38, Q39, Q40, Q41, Q42, Q43, Q44, Q45, Q46, Q47, Q48, Q49, Q50, Q51, Q52, Q53, Q54, Q55, Q56, Q57, Q58, Q59, Q60, Q61, Q62, Q63, Q64, Q65]), "depth" : 2 * mm, "offsetDistance" : 25 * mm});
        }
    });
